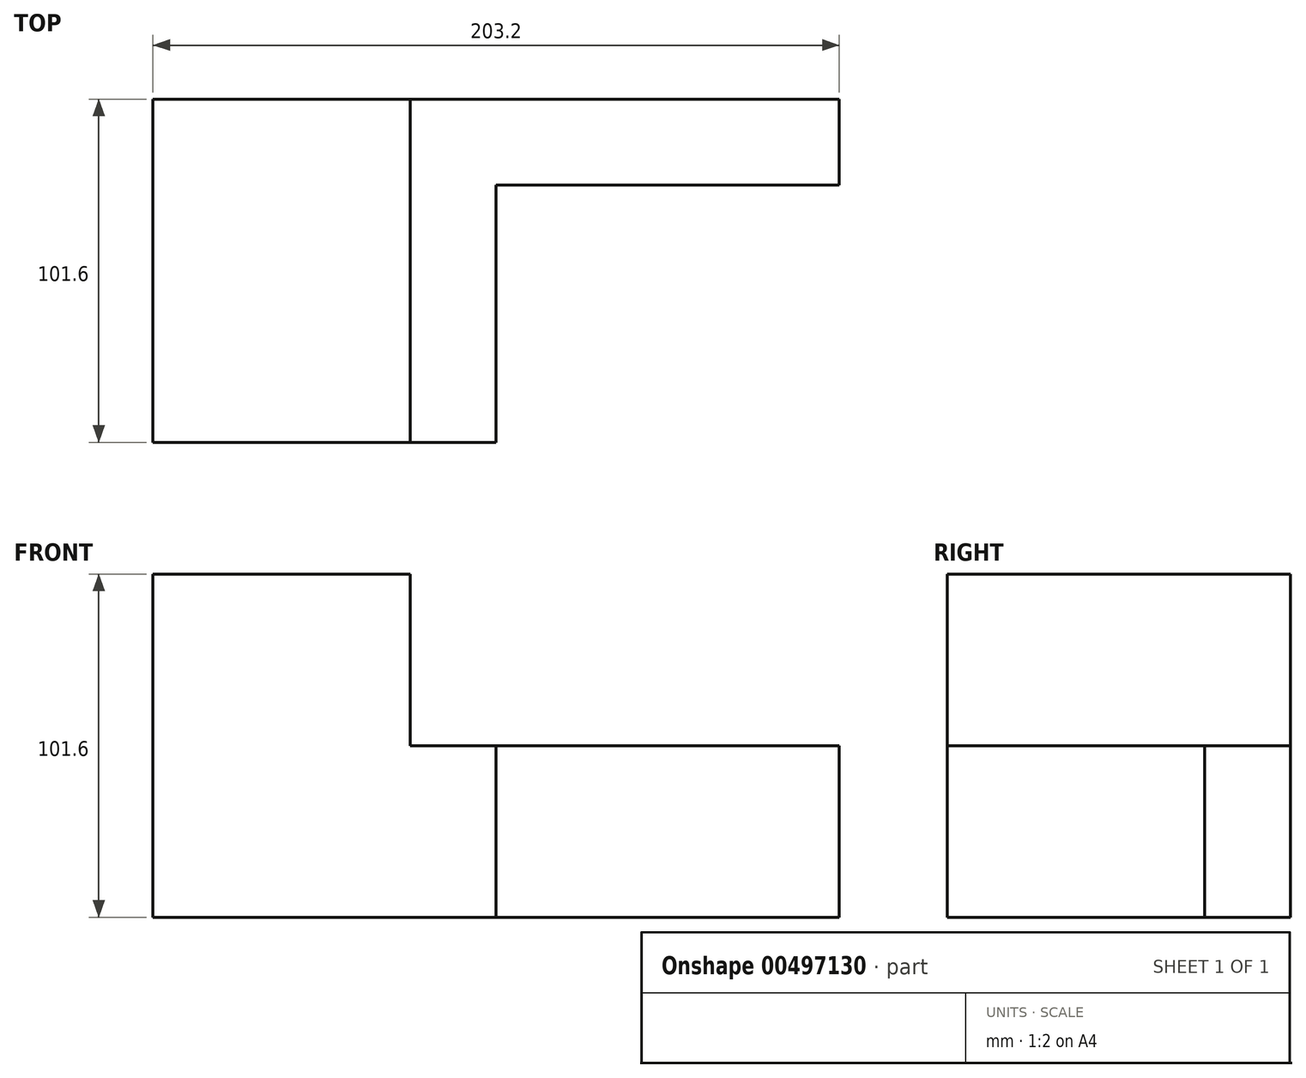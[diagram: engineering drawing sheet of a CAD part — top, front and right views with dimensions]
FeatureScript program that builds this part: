
annotation { "Feature Type Name" : "Feature", "Feature Type Description" : "" }
export const myFeature = defineFeature(function(context is Context, id is Id, definition is map)
    precondition{}
    {
        {
            var Q0;
            Q0=qCreatedBy(makeId("Top.planeOp"),FACE);
            var sketch = newSketch(context, id + "F0", { "sketchPlane" : qUnion([Q0])});
            skLineSegment(sketch, "E0.bottom", {"start": v(0, 0) * mm, "end": v(-76.2, 0) * mm});
            skLineSegment(sketch, "E0.top", {"start": v(0, 101.6) * mm, "end": v(-76.2, 101.6) * mm});
            skLineSegment(sketch, "E0.left", {"start": v(0, 0) * mm, "end": v(0, 101.6) * mm});
            skLineSegment(sketch, "E0.right", {"start": v(-76.2, 0) * mm, "end": v(-76.2, 101.6) * mm});
            skLineSegment(sketch, "E1.bottom", {"start": v(0, 0) * mm, "end": v(25.4, 0) * mm});
            skLineSegment(sketch, "E1.top", {"start": v(0, 76.2) * mm, "end": v(25.4, 76.2) * mm});
            skLineSegment(sketch, "E1.left", {"start": v(0, 0) * mm, "end": v(0, 76.2) * mm});
            skLineSegment(sketch, "E1.right", {"start": v(25.4, 0) * mm, "end": v(25.4, 76.2) * mm});
            skPoint(sketch, "E2.oppositeSnap0", {"position": v(12.7, 76.2) * mm});
            skLineSegment(sketch, "E2.bottom", {"start": v(0, 101.6) * mm, "end": v(127, 101.6) * mm});
            skLineSegment(sketch, "E2.top", {"start": v(0, 76.2) * mm, "end": v(127, 76.2) * mm});
            skLineSegment(sketch, "E2.left", {"start": v(0, 101.6) * mm, "end": v(0, 76.2) * mm});
            skLineSegment(sketch, "E2.right", {"start": v(127, 101.6) * mm, "end": v(127, 76.2) * mm});
            skSolve(sketch);
        }
        {
            var Q0;
            Q0=makeQuery(id+"F0.imprint","IMPRINT",FACE,{"disambiguationData":[TD([[makeQuery(id+"F0.imprint","IMPRINT",EDGE,{"derivedFrom":sQuery(id+"F0.wireOp",EDGE,"E0.bottom")}),-1.0]])]});
            extrude(context, id + "F1", {"entities" : qUnion([Q0]), "depth" : 101.6 * mm});
        }
        {
            var Q0;
            Q0=makeQuery(id+"F0.imprint","IMPRINT",FACE,{"disambiguationData":[TD([[makeQuery(id+"F0.imprint","IMPRINT",EDGE,{"derivedFrom":sQuery(id+"F0.wireOp",EDGE,"E1.bottom")}),1.0]])]});
            var Q1;
            Q1=makeQuery(id+"F0.imprint","IMPRINT",FACE,{"disambiguationData":[TD([[makeQuery(id+"F0.imprint","IMPRINT",EDGE,{"derivedFrom":sQuery(id+"F0.wireOp",EDGE,"E2.bottom")}),-1.0]])]});
            extrude(context, id + "F2", {"entities" : qUnion([Q0, Q1]), "operationType" : NewBodyOperationType.ADD, "depth" : 50.8 * mm});
        }
    });
